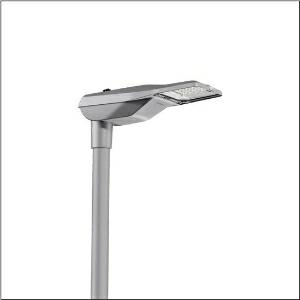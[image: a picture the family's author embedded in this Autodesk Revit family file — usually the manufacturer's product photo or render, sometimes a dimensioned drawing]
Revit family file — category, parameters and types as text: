
# Revit family: streetlight_sl_21_iq_micro___p0_8ab_5xe1r31v08db_6cb1
name_source: partatom
category: Lighting Fixtures
units: mm (PartAtom-declared; Revit-internal decimal feet)

## family parameters
Cut with Voids When Loaded = No
Host = Face
Light Source = No
Part Type = Normal
Room Calculation Point = No
Round Connector Dimension = Use Diameter
Shared = No

## types (1)
- --- (1 x LED, 4550 lm, 39.1 W, 3000K)
    Apparent Load = 39 VA
    CIE Flux Codes = 36 71 98 100 100
    Color Rendering = 70
    Color Temperature = 3000K
    Default Elevation = 1800 mm
    Description = Streetlight SL 21 iQ micro, mast luminaire, primary light control with lens, of PMMA, primary optical cover: cover, of toughened safety glass, transparent, light distribution: P0.8aB, light emission: direct distribution, primary light characteristic: asymmetric, installation type: post-top, side-entry, LED, High Power LED, rated luminous flux: 4.550lm, luminous efficacy: 116lm/W, light colour: 730, colour temperature: 3000K, control gear: iQ-Street Remote, D4i with power reduction, control: pre-setting: logarithmic dimming characteristic, Street-Remote, Auto-Match, Temp-Guard, Lumen-Switch, Night-Set, Smart-Wire, Light-Fading, Desk-Remote (wireless, voltage-free reading and setting of iQ features in the workshop via application-optimized NFC function/RFID function), optimised constant luminous flux control (CLO 2.0), mains connection: 220..240V, AC, 50/60Hz, start of lifetime: 39W, end of service life: 41W, reduction: 17W, luminaire housing, of diecast aluminium, powder-coated, SITECO metallic grey (DB 702S), corrosivity category C5 high according to DIN EN ISO 12944, please order mast flange separately, inclination adjustable: 0°, 5°, 10°, 15°, sealing non-destructively replaceable, multi-level sealing system, length: 528mm, width: 235mm, height: 110mm, mast flange for spigot size: 42mm (side-entry): 5XC10008XM4, 60/48mm (side-entry/post-top): 5XC10108XM2, 76/60mm (side-entry/post-top): 5XC10108XM1, mounting height: 4..8m, Smart Interface above, protection rating (complete): IP66, insulation class (complete): insulation class II (safety insulation), certification: CE, ENEC, ENEC+, VDE, impact resistance: IK10, permissible operating ambient temperature for outdoor applications: -40..+50°C, standard-compliant lighting for roads and squares, packaging unit: 1 piece

Light Distribution: P0.8aB
    Height = 110 mm
    Lamp = 1 x LED
    Lamp Light Flux = 4550 lm
    Lamp Power = 39.1 W
    Lamp count = 1
    Length = 528 mm
    Luminous efficacy = 116 lm/W
    Manufacturer = Siteco
    ModVariant = No
    Model = 5XE1R31V08DB
    Number of Poles = 1
    OnlyDefault = Yes
    Power Factor = 1
    Product Name = Streetlight SL 21 iQ micro | P0.8aB
    Product group = mast luminaire | pylon top
    ProductGroupID = 6100
    Protection Class = Protection class II
    Protection Degree = IP 66
    RLX_Detail_Level = 1
    RLX_Emergency_Light_Flux = 0 lm
    RLX_Emergency_Type = 0
    RLX_Emergency_Type_DB = No
    RlxData = <blob elided: 98741 chars, md5=361c666f>
    Socket = socket
    Standby Power = 0 W
    System Light Flux = 4550 lm
    System Power = 39 W
    Type Comments = factory setting: luminous flux: 100 % | dim-lin: 254 | 765 mA
    Type Image = l_1277292.jpg
    URL = http://relux.com
    VarID = @adj_083361
    Voltage = 0 V
    Weight = 0.00 kg
    Width = 235 mm

## geometry (parser evidence)
native form markers: Blend x4, Sweep x11
no freeform markers — native parametric forms only
